# Revit family: Hager-FW-Hollow_wall-IP30-With_Cover-With_DIN-Hosted-CH-it
name_source: partatom
category: Electrical Equipment
units: mm (PartAtom-declared; Revit-internal decimal feet)

## family parameters
Cut with Voids When Loaded = No
Host = Face
Maintain Annotation Orientation = Yes
Panel Configuration = Two Columns, Circuits Across
Part Type = Panelboard
Room Calculation Point = No
Round Connector Dimension = Use Diameter
Shared = No

## types (5) — shared parameters
BC_MODEL_ID = 1554225
BC_OBJECT_ID = 513831
BC_OBJECT_VERSION = #9
Code hager = ADD-EC000214_EU
EF000003 - modo di montaggio = parete forata
EF000007 - colore = bianco
EF000024 - resistente ai raggi UV = No
EF000049 - profondità = 125 mm  [stored 0.410105 ft]
EF000116 - numero RAL = 9010
EF000118 - con piastra di montaggio = Yes
EF000218 - profondità di montaggio = 112 mm  [stored 0.367454 ft]
EF001062 - versione EMC = No
EF001088 - possibilità di applicazione = Yes
EF001134 - barra DIN = Yes
EF002950 - numero di unità modulari = 12
EF004462 - tipo di chiusura = altri
EF005474 - grado di protezione (IP) = IP30
EF006244 - coperchio/porta trasparente = No
EF006306 - con serratura = No
EF009212 - tipo di coperchio = con taglio
EF015776 - morsetto di messa a terra = No
EF015777 - morsettiera a conduttore neutro = No
EF015941 - porta di trasmissione del segnale = No
ETIM class code = EC000214
ETIM class name = Small distribution board
HG000002-with door or cover-it = Yes
HG000003-Range-it = FW
HG000005-Thickness-it = 2 mm  [stored 0.00656168 ft]
HG000006-Flush mounted-it = Yes
HG000007-Number of empty columns-it = 1
HG000011-Empty rows from bottom-it = No
HG000012-Door swing angle-it = 90.00°
HG000013-Door on the left-it = No
HG000014-Door on the right-it = Yes
HG000015-Clearance visibility-it = Yes
HG000016-Door 3D visibility-it = Yes
HG000017-Distance between poles-it = 18 mm  [stored 0.0590551 ft]
HG000060-RAL-number = 9010
HG000099-Onfly Template ID-it-CH = 507532
HGEF0002950-larghezza in unità di suddivisione = 12
Manufacturer = Hager
Name = FW-Hollow_wall-IP30-With_Cover-With_DIN-CH
Name BIM&CO = Electricity
Name hager = ADD_Enclosures_EC000214
Uniformat = Low Tension Service & Dist.
Uniformat code = D501001
zero-valued in all types: Default Elevation, EF001131 - profondità interna

## per-type parameters (varying)
| type | BC_VARIANT_ID | EF000008 - larghezza | EF000040 - altezza | EF000266 - numero di file | EF000332 - altezza di installazione | EF000846 - larghezza di montaggio | HG000001 - Numero di colonne | HG000004-Manufacturer reference-it | HG000008-Number of empty rows-it | HG000009-Double swing door-it | HG000010-Asymmetric doors-it | HGEF000266-Numero di file |
| FW-Hollow_wall_W603_H703_D125_12_Modular_Spacing-FWU42K | 1178612 | 603 mm | 703 mm  [stored 2.30643 ft] | 4 | 652 mm  [stored 2.13911 ft] | 560 mm  [stored 1.83727 ft] | 1 | FWU42K | 4 | No | No | 4 |
| FW-Hollow_wall_W853_H703_D125_12_Modular_Spacing-FWU43K | 1178613 | 853 mm  [stored 2.79856 ft] | 703 mm  [stored 2.30643 ft] | 4 | 652 mm  [stored 2.13911 ft] | 810 mm | 2 | FWU43K | 4 | Yes | Yes | 4 |
| FW-Hollow_wall_W603_H853_D125_12_Modular_Spacing-FWU52K | 1178614 | 603 mm | 853 mm  [stored 2.79856 ft] | 5 | 802 mm  [stored 2.63123 ft] | 560 mm  [stored 1.83727 ft] | 1 | FWU52K | 5 | No | No | 5 |
| FW-Hollow_wall_W853_H853_D125_12_Modular_Spacing-FWU53K | 1178615 | 853 mm  [stored 2.79856 ft] | 853 mm  [stored 2.79856 ft] | 5 | 802 mm  [stored 2.63123 ft] | 810 mm | 2 | FWU53K | 5 | Yes | Yes | 5 |
| FW-Hollow_wall_W603_H1003_D125_12_Modular_Spacing-FWU62K | 1178616 | 603 mm | 1003 mm  [stored 3.29068 ft] | 6 | 952 mm  [stored 3.12336 ft] | 560 mm  [stored 1.83727 ft] | 1 | FWU62K | 6 | No | No | 6 |

note: column(s) folded — value = type name in every type: Reference

note: [stored X ft] marks values corroborated as IEEE doubles in the binary element streams (Revit-internal decimal feet)

## geometry (parser evidence)
native form markers: Sweep x14
no freeform markers — native parametric forms only
